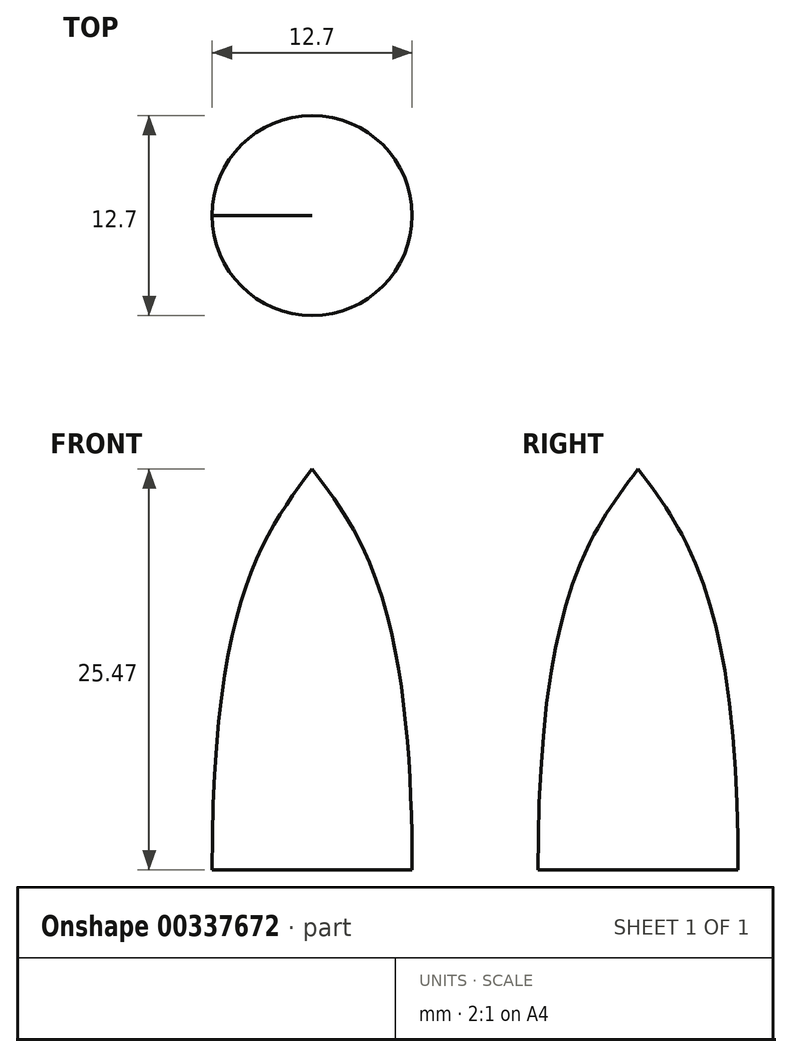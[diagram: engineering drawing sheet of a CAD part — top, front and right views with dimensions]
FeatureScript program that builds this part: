
annotation { "Feature Type Name" : "Feature", "Feature Type Description" : "" }
export const myFeature = defineFeature(function(context is Context, id is Id, definition is map)
    precondition{}
    {
        {
            var Q0;
            Q0=qCreatedBy(makeId("Top.planeOp"),FACE);
            var sketch = newSketch(context, id + "F0", { "sketchPlane" : qUnion([Q0])});
            skCircle(sketch, "E0", {"center": v(0, 0) * mm, "radius": 6.35 * mm});
            skSolve(sketch);
        }
        {
            var Q0;
            Q0=qCreatedBy(makeId("Top.planeOp"),FACE);
            cPlane(context, id + "F1", {"entities" : qUnion([Q0]), "cplaneType" : CPlaneType.OFFSET, "offset" : 25.4 * mm, "width" : 152.4 * mm, "height" : 152.4 * mm});
        }
        {
            var Q0;
            Q0=qCreatedBy(makeId("Front.planeOp"),FACE);
            var sketch = newSketch(context, id + "F2", { "sketchPlane" : qUnion([Q0])});
            skFitSpline(sketch, "E1", {"points": [v(0, 0) * mm, v(0, 14.4) * mm, v(0, 25.47) * mm, v(0, 25.58) * mm], "startDerivative": vector(0.68, 28.49) * mm, "endDerivative": vector(0.64, 1.57) * mm});
            skSolve(sketch);
        }
        {
            var Q0;
            Q0=makeQuery(id+"F0.imprint","IMPRINT",FACE,{"disambiguationData":[TD([[makeQuery(id+"F0.imprint","IMPRINT",EDGE,{"derivedFrom":sQuery(id+"F0.wireOp",EDGE,"E0")}),1.0]])]});
            var Q1;
            Q1=sQuery(id+"F2.wireOp",VERTEX,"E1.2.internal");
            loft(context, id + "F3", {"startCondition" : LoftEndDerivativeType.NORMAL_TO_PROFILE, "startMagnitude" : 2, "sheetProfilesArray" : [{ "sheetProfileEntities" : qUnion([Q0]) }, { "sheetProfileEntities" : qUnion([Q1]) }]});
        }
    });
